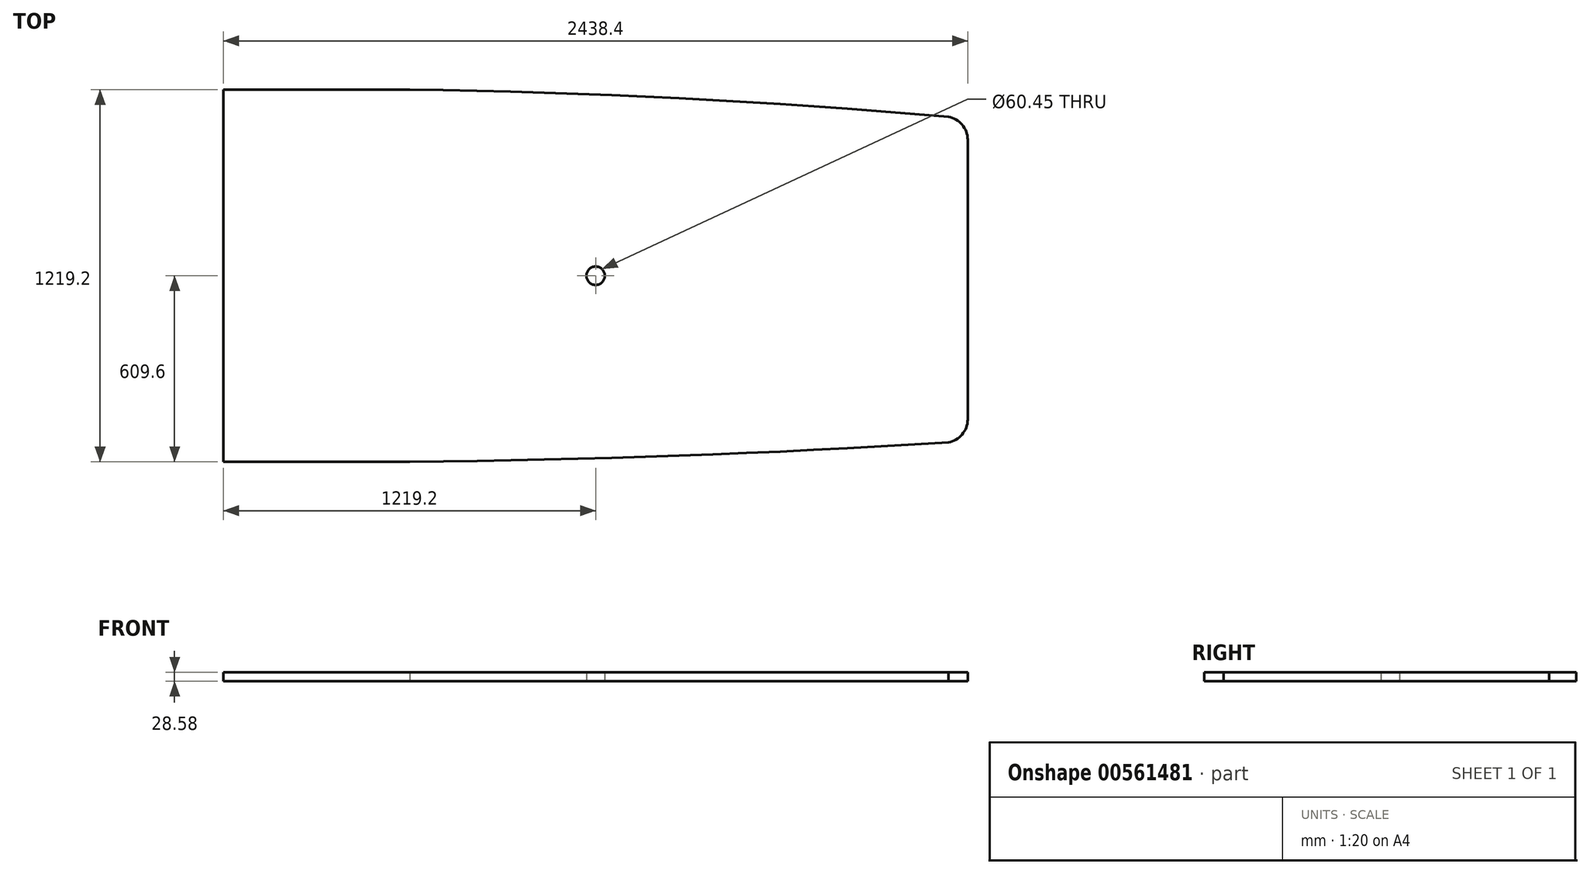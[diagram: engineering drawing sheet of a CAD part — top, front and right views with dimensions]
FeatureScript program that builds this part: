
annotation { "Feature Type Name" : "Feature", "Feature Type Description" : "" }
export const myFeature = defineFeature(function(context is Context, id is Id, definition is map)
    precondition{}
    {
        {
            var Q0;
            Q0=qCreatedBy(makeId("Top.planeOp"),FACE);
            var sketch = newSketch(context, id + "F0", { "sketchPlane" : qUnion([Q0])});
            skLineSegment(sketch, "E0.left", {"start": v(1219.2, 445.57) * mm, "end": v(1219.2, -470.97) * mm});
            skPoint(sketch, "E0.middle", {"position": v(0, 0) * mm});
            skPoint(sketch, "E1.visualSharp", {"position": v(1219.2, 533.4) * mm});
            skArc(sketch, "E1.filletArc", {"start": v(1219.2, 445.57) * mm, "mid": v(1201.2, 494.75) * mm, "end": v(1155.7, 520.7) * mm});
            skPoint(sketch, "E2.visualSharp", {"position": v(1219.2, -533.4) * mm});
            skArc(sketch, "E2.filletArc", {"start": v(1155.7, -546.1) * mm, "mid": v(1201.2, -520.15) * mm, "end": v(1219.2, -470.97) * mm});
            skLineSegment(sketch, "E3", {"start": v(-1219.2, -609.6) * mm, "end": v(1155.7, -546.1) * mm});
            skLineSegment(sketch, "E4", {"start": v(-1219.2, 609.6) * mm, "end": v(1155.7, 520.7) * mm});
            skLineSegment(sketch, "E5", {"start": v(-1219.2, 609.6) * mm, "end": v(-1219.2, -609.6) * mm});
            skCircle(sketch, "E6", {"center": v(0, 0) * mm, "radius": 30.23 * mm});
            skLineSegment(sketch, "E7", {"start": v(-1219.2, 609.6) * mm, "end": v(-609.6, 609.6) * mm});
            skLineSegment(sketch, "E8", {"start": v(-1219.2, -609.6) * mm, "end": v(-609.6, -609.6) * mm});
            skArc(sketch, "E9", {"start": v(1155.7, 520.7) * mm, "mid": v(-30.63, 595.03) * mm, "end": v(-1219.2, 609.6) * mm});
            skArc(sketch, "E10", {"start": v(-1219.2, -609.6) * mm, "mid": v(-31.18, -599.2) * mm, "end": v(1155.7, -546.1) * mm});
            skSolve(sketch);
        }
        {
            var Q0;
            Q0=makeQuery(id+"F0.imprint","IMPRINT",FACE,{"disambiguationData":[TD([[makeQuery(id+"F0.imprint","IMPRINT",EDGE,{"derivedFrom":sQuery(id+"F0.wireOp",EDGE,"E0.left")}),-1.0]])]});
            var Q1;
            {var subQ0=sQuery(id+"F0.wireOp",EDGE,"E4");Q1=makeQuery(id+"F0.imprint","IMPRINT",FACE,{"disambiguationData":[TD([[makeQuery(id+"F0.imprint","IMPRINT",EDGE,{"derivedFrom":subQ0}),1.0]])]});}
            var Q2;
            {var subQ0=sQuery(id+"F0.wireOp",EDGE,"E3");Q2=makeQuery(id+"F0.imprint","IMPRINT",FACE,{"disambiguationData":[TD([[makeQuery(id+"F0.imprint","IMPRINT",EDGE,{"derivedFrom":subQ0}),-1.0]])]});}
            extrude(context, id + "F1", {"entities" : qUnion([Q0, Q1, Q2]), "depth" : 28.57 * mm, "offsetDistance" : 25.4 * mm});
        }
    });
